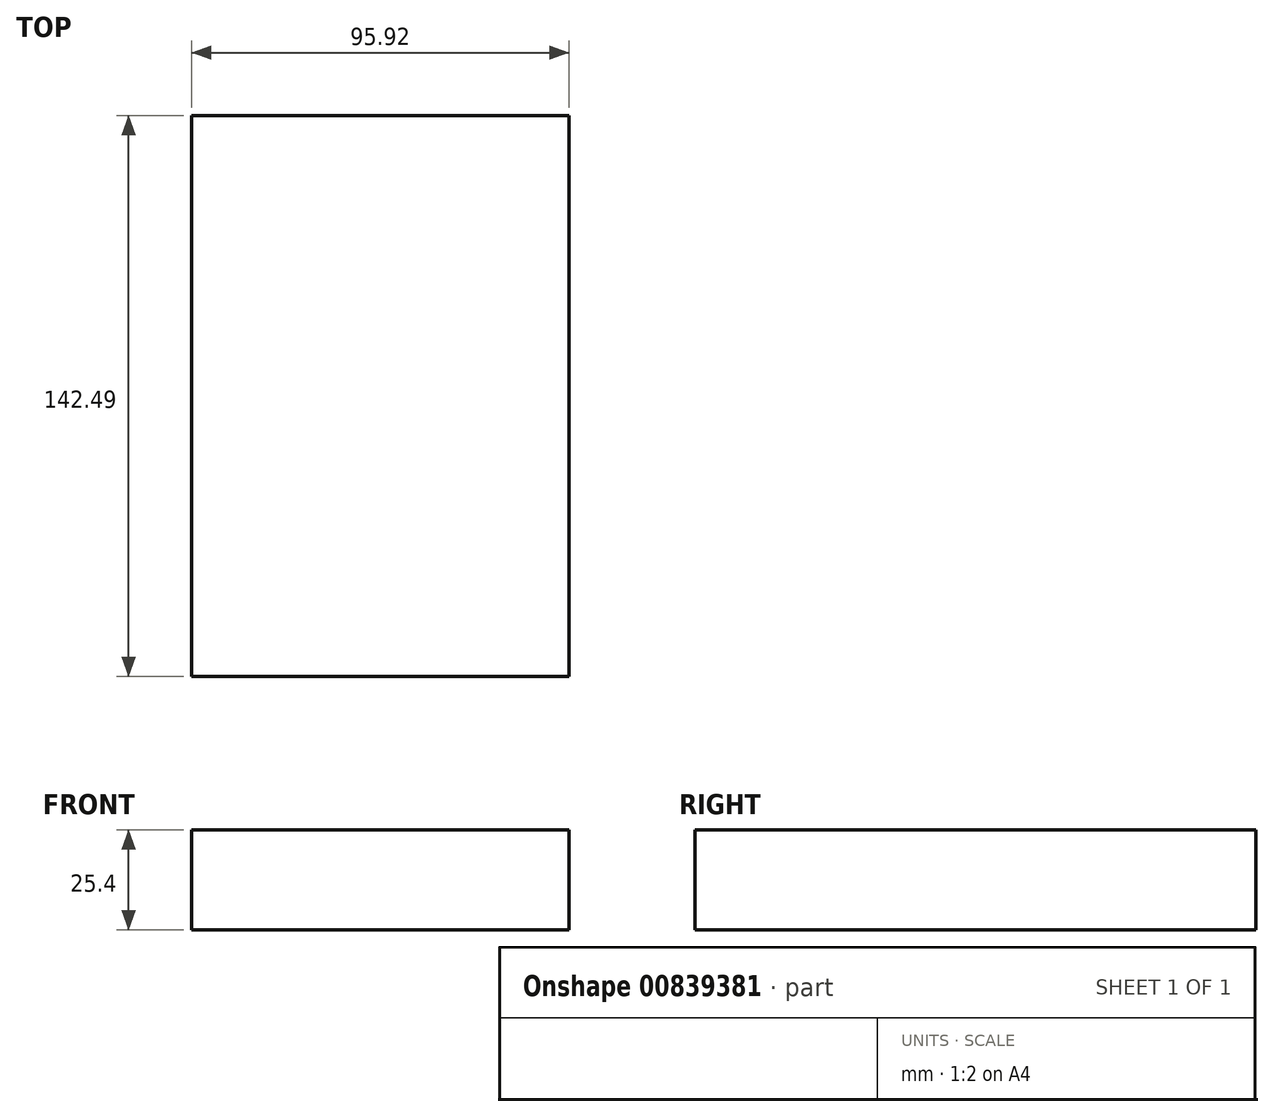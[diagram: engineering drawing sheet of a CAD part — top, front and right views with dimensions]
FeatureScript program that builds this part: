
annotation { "Feature Type Name" : "Feature", "Feature Type Description" : "" }
export const myFeature = defineFeature(function(context is Context, id is Id, definition is map)
    precondition{}
    {
        {
            var Q0;
            Q0=qCreatedBy(makeId("Top.planeOp"),FACE);
            var sketch = newSketch(context, id + "F0", { "sketchPlane" : qUnion([Q0])});
            skLineSegment(sketch, "E0.bottom", {"start": v(8.35, 90.1) * mm, "end": v(104.27, 90.1) * mm});
            skLineSegment(sketch, "E0.top", {"start": v(8.35, -52.39) * mm, "end": v(104.27, -52.39) * mm});
            skLineSegment(sketch, "E0.left", {"start": v(8.35, 90.1) * mm, "end": v(8.35, -52.39) * mm});
            skLineSegment(sketch, "E0.right", {"start": v(104.27, 90.1) * mm, "end": v(104.27, -52.39) * mm});
            skSolve(sketch);
        }
        {
            var Q0;
            Q0 = qSketchRegion(id + "F0", true);
            extrude(context, id + "F1", {"entities" : qUnion([Q0]), "depth" : 25.4 * mm, "offsetDistance" : 25.4 * mm});
        }
    });
